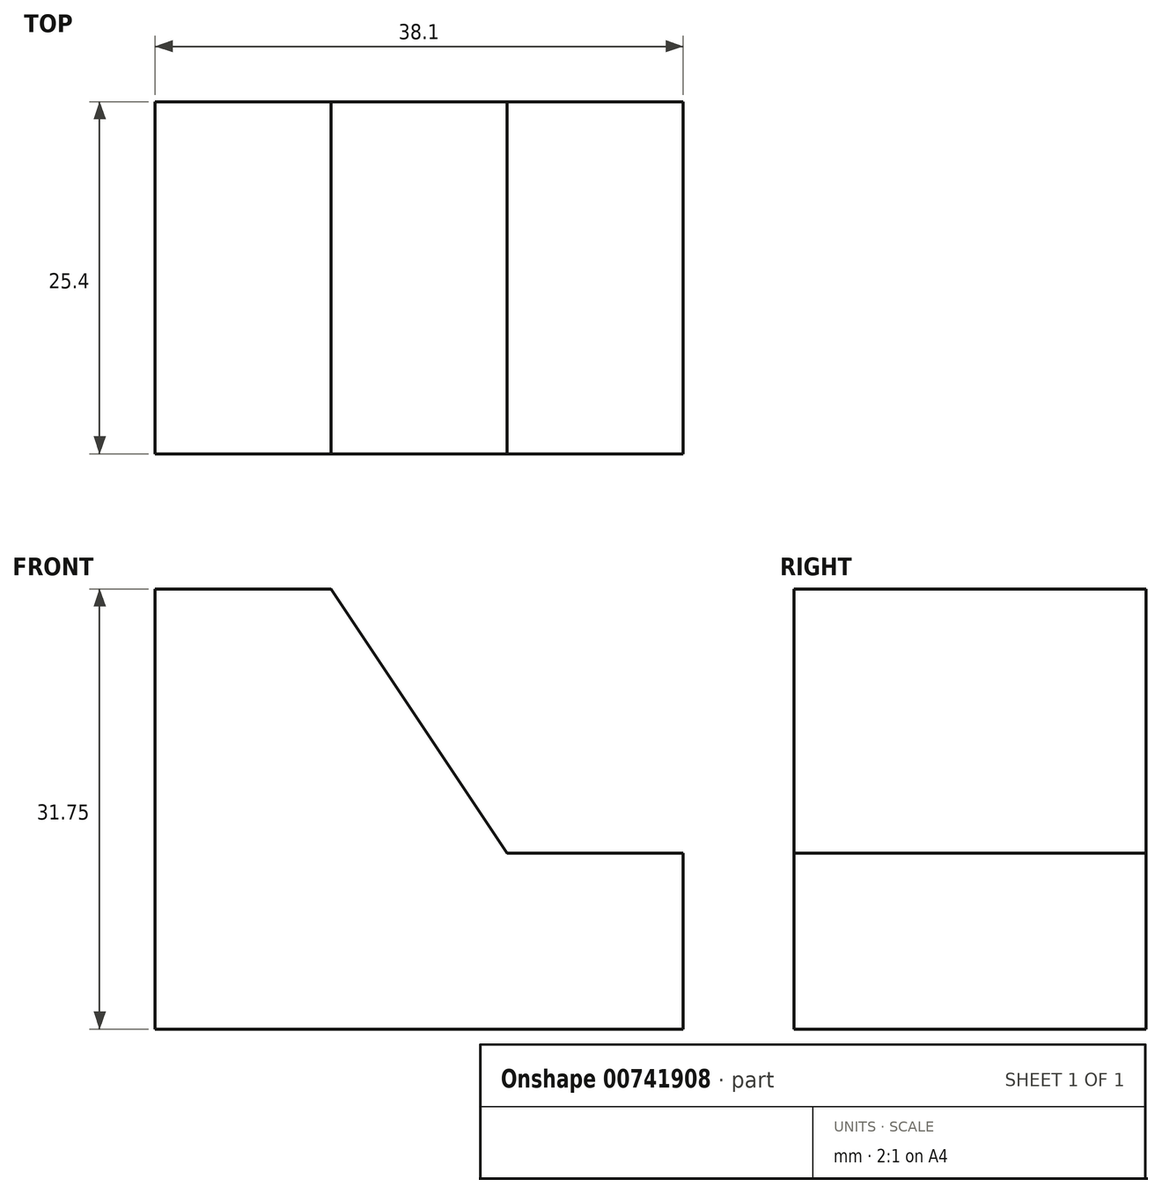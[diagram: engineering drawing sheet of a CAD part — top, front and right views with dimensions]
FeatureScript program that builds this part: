
annotation { "Feature Type Name" : "Feature", "Feature Type Description" : "" }
export const myFeature = defineFeature(function(context is Context, id is Id, definition is map)
    precondition{}
    {
        {
            var Q0;
            Q0=qCreatedBy(makeId("Front.planeOp"),FACE);
            var sketch = newSketch(context, id + "F0", { "sketchPlane" : qUnion([Q0])});
            skLineSegment(sketch, "E0", {"start": v(0, 31.75) * mm, "end": v(0, 0) * mm});
            skLineSegment(sketch, "E1", {"start": v(0, 0) * mm, "end": v(38.1, 0) * mm});
            skLineSegment(sketch, "E2", {"start": v(38.1, 0) * mm, "end": v(38.1, 12.7) * mm});
            skLineSegment(sketch, "E3", {"start": v(38.1, 12.7) * mm, "end": v(25.4, 12.7) * mm});
            skLineSegment(sketch, "E4", {"start": v(0, 31.75) * mm, "end": v(12.7, 31.75) * mm});
            skLineSegment(sketch, "E5", {"start": v(12.7, 31.75) * mm, "end": v(25.4, 12.7) * mm});
            skSolve(sketch);
        }
        {
            var Q0;
            Q0=makeQuery(id+"F0.imprint","IMPRINT",FACE,{"disambiguationData":[TD([[makeQuery(id+"F0.imprint","IMPRINT",EDGE,{"derivedFrom":sQuery(id+"F0.wireOp",EDGE,"E0")}),1.0]])]});
            extrude(context, id + "F1", {"entities" : qUnion([Q0]), "depth" : 25.4 * mm, "offsetDistance" : 25.4 * mm});
        }
    });
